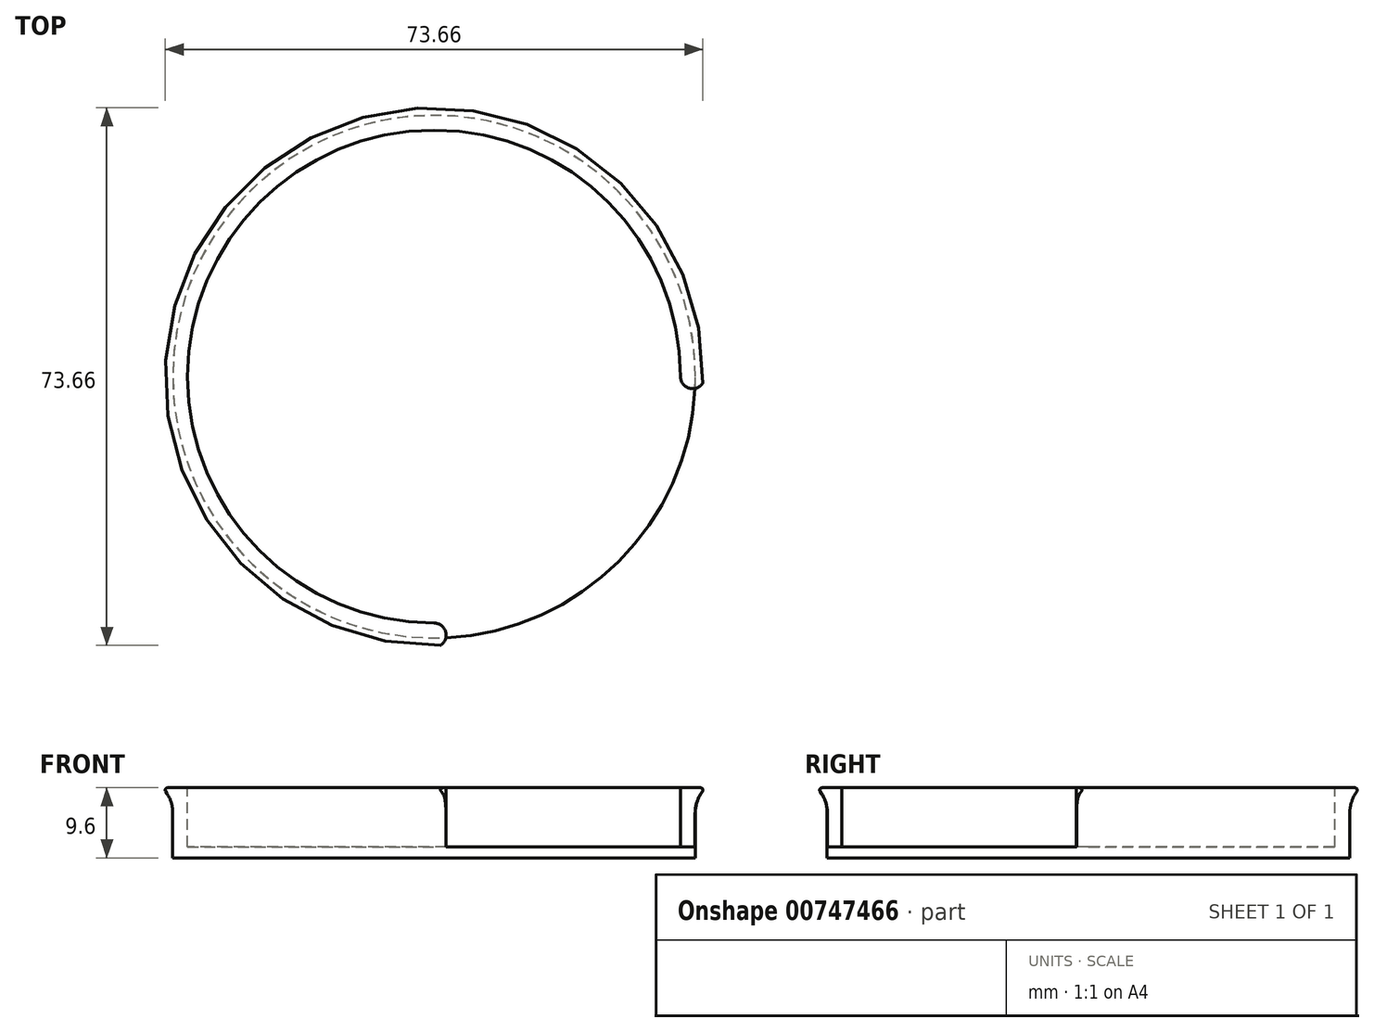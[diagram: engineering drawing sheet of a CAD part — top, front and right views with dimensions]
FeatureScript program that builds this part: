
annotation { "Feature Type Name" : "Feature", "Feature Type Description" : "" }
export const myFeature = defineFeature(function(context is Context, id is Id, definition is map)
    precondition{}
    {
        {
            var Q0;
            Q0=qCreatedBy(makeId("Right.planeOp"),FACE);
            var sketch = newSketch(context, id + "F0", { "sketchPlane" : qUnion([Q0])});
            skLineSegment(sketch, "E0", {"start": v(-27.34, 9.6) * mm, "end": v(-27.34, 0) * mm});
            skLineSegment(sketch, "E1", {"start": v(-27.34, 9.6) * mm, "end": v(-64.4, 9.6) * mm});
            skLineSegment(sketch, "E2", {"start": v(-27.34, 0) * mm, "end": v(-63.14, 0) * mm});
            skLineSegment(sketch, "E3", {"start": v(-63.14, 0) * mm, "end": v(-63.14, 7.57) * mm});
            skLineSegment(sketch, "E4", {"start": v(-63.14, 7.57) * mm, "end": v(-63.14, 9.6) * mm});
            skLineSegment(sketch, "E5", {"start": v(-64.4, 9.6) * mm, "end": v(-63.14, 7.57) * mm});
            skSolve(sketch);
        }
        {
            var Q0;
            Q0=qSketchRegion(id+"F0",true);
            var Q1;
            Q1=sQuery(id+"F0.wireOp",EDGE,"E0");
            revolve(context, id + "F1", {"entities" : qUnion([Q0]), "axis" : qUnion([Q1]), "revolveType" : RevolveType.FULL});
        }
        {
            var Q0;
            Q0=makeQuery(id+"F1.opRevolve","SWEPT_FACE",FACE,{"disambiguationData":[OSD([sQuery(id+"F0.wireOp",EDGE,"E1")])]});
            var sketch = newSketch(context, id + "F2", { "sketchPlane" : qUnion([Q0])});
            skCircle(sketch, "E6", {"center": v(0, -27.34) * mm, "radius": 33.77 * mm});
            skLineSegment(sketch, "E7.bottom", {"start": v(0, -27.34) * mm, "end": v(37.07, -27.34) * mm});
            skLineSegment(sketch, "E7.top", {"start": v(0, -64.4) * mm, "end": v(37.07, -64.4) * mm});
            skLineSegment(sketch, "E7.left", {"start": v(0, -27.34) * mm, "end": v(0, -64.4) * mm});
            skLineSegment(sketch, "E7.right", {"start": v(37.07, -27.34) * mm, "end": v(37.07, -64.4) * mm});
            skArc(sketch, "E8", {"start": v(0, -64.4) * mm, "mid": v(1.65, -62.76) * mm, "end": v(0, -61.1) * mm});
            skArc(sketch, "E9", {"start": v(33.77, -27.34) * mm, "mid": v(35.42, -28.99) * mm, "end": v(37.07, -27.34) * mm});
            skSolve(sketch);
        }
        {
            var Q0;
            {var subQ0=sQuery(id+"F2.wireOp",EDGE,"E7.left");var subQ3=sQuery(id+"F2.wireOp",EDGE,"E7.bottom");var subQ5=makeQuery(id+"F2.imprint","INTERSECT",VERTEX,{"derivedFrom":[subQ3,subQ0]});Q0=makeQuery(id+"F2.imprint","IMPRINT",FACE,{"disambiguationData":[TD([[makeQuery(id+"F2.imprint","IMPRINT",EDGE,{"disambiguationData":[TD([[subQ5,-1.0]])],"derivedFrom":subQ3}),1.0]])]});}
            var Q1;
            {var subQ0=sQuery(id+"F2.wireOp",EDGE,"E7.left");var subQ3=sQuery(id+"F2.wireOp",EDGE,"E7.bottom");var subQ5=makeQuery(id+"F2.imprint","INTERSECT",VERTEX,{"derivedFrom":[subQ3,subQ0]});Q1=makeQuery(id+"F2.imprint","IMPRINT",FACE,{"disambiguationData":[TD([[makeQuery(id+"F2.imprint","IMPRINT",EDGE,{"disambiguationData":[TD([[subQ5,-1.0]])],"derivedFrom":subQ3}),-1.0]])]});}
            var Q2;
            {var subQ0=sQuery(id+"F2.wireOp",EDGE,"E8");Q2=makeQuery(id+"F2.imprint","IMPRINT",FACE,{"disambiguationData":[TD([[makeQuery(id+"F2.imprint","IMPRINT",EDGE,{"derivedFrom":subQ0}),-1.0]])]});}
            extrude(context, id + "F3", {"entities" : qUnion([Q0, Q1, Q2]), "operationType" : NewBodyOperationType.REMOVE, "oppositeDirection" : true, "depth" : 8.08 * mm});
        }
        {
            var Q0;
            Q0=makeQuery(id+"F1.opRevolve","SWEPT_EDGE",EDGE,{"disambiguationData":[OSD([sQuery(id+"F0.wireOp",EDGE,"E1"),sQuery(id+"F0.wireOp",EDGE,"E5")])]});
            var Q1;
            Q1=makeQuery(id+"F3.boolean.opBoolean","COPY",EDGE,{"derivedFrom":makeQuery(id+"F3.opExtrude","CAP_EDGE",EDGE,{"disambiguationData":[OSD([sQuery(id+"F2.wireOp",EDGE,"E6")])],"isStart":true})});
            fillet(context, id + "F4", {"entities" : qUnion([Q0, Q1]), "radius" : 0.3 * mm, "tangentPropagation" : true, "allowEdgeOverflow" : false});
        }
        {
            var Q0;
            Q0=makeQuery(id+"F1.opRevolve","SWEPT_EDGE",EDGE,{"disambiguationData":[OSD([sQuery(id+"F0.wireOp",EDGE,"E3"),sQuery(id+"F0.wireOp",EDGE,"E4"),sQuery(id+"F0.wireOp",EDGE,"E5")])]});
            fillet(context, id + "F5", {"entities" : qUnion([Q0]), "radius" : 5 * mm, "tangentPropagation" : true, "allowEdgeOverflow" : false});
        }
    });
